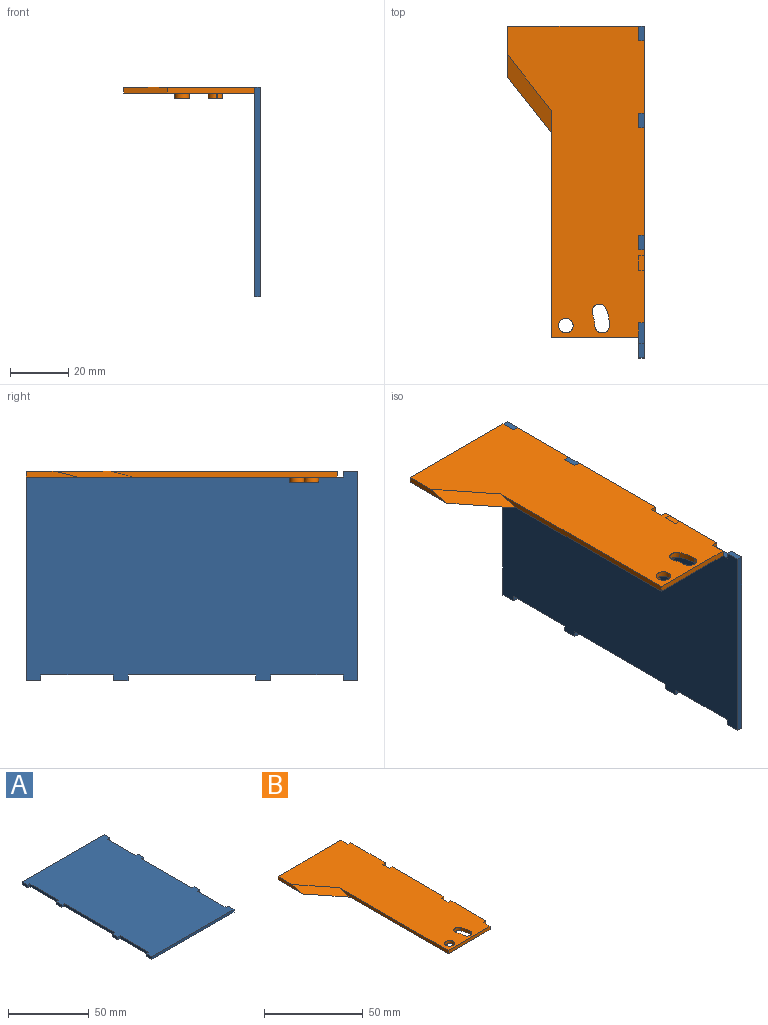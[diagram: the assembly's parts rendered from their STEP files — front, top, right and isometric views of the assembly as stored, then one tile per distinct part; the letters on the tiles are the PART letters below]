
ASSEMBLY  parts=2 mates=1
PART A: 30 faces, bbox 72x114x2 mm
  f0: plane 2x2mm, normal (0,1,0), area 4mm2, adj f1,f27,f28,f29
  f1: plane 44x2mm, normal (1,0,0), area 88mm2, adj f0,f2,f28,f29
  f2: plane 2x2mm, normal (0,-1,0), area 4mm2, adj f1,f3,f28,f29
  f3: plane 5x2mm, normal (1,0,0), area 10mm2, adj f2,f4,f28,f29
  f4: plane 2x2mm, normal (0,1,0), area 4mm2, adj f3,f5,f28,f29
  f5: plane 25x2mm, normal (1,0,0), area 50mm2, adj f4,f6,f28,f29
  f6: plane 2x2mm, normal (0,-1,0), area 4mm2, adj f5,f7,f28,f29
  f7: plane 5x2mm, normal (1,0,0), area 10mm2, adj f6,f8,f28,f29
  f8: plane 72x2mm, normal (0,1,0), area 144mm2, adj f7,f9,f28,f29
  f9: plane 5x2mm, normal (-1,0,0), area 10mm2, adj f8,f10,f28,f29
  f10: plane 2x2mm, normal (0,-1,0), area 4mm2, adj f9,f11,f28,f29
  f11: plane 25x2mm, normal (-1,0,0), area 50mm2, adj f10,f12,f28,f29
  f12: plane 2x2mm, normal (0,1,0), area 4mm2, adj f11,f13,f28,f29
  f13: plane 5x2mm, normal (-1,0,0), area 10mm2, adj f12,f14,f28,f29
  f14: plane 2x2mm, normal (0,-1,0), area 4mm2, adj f13,f15,f28,f29
  f15: plane 44x2mm, normal (-1,0,0), area 88mm2, adj f14,f16,f28,f29
  f16: plane 2x2mm, normal (0,1,0), area 4mm2, adj f15,f17,f28,f29
  f17: plane 5x2mm, normal (-1,0,0), area 10mm2, adj f16,f18,f28,f29
  f18: plane 2x2mm, normal (0,-1,0), area 4mm2, adj f17,f19,f28,f29
  f19: plane 25x2mm, normal (-1,0,0), area 50mm2, adj f18,f20,f28,f29
  f20: plane 2x2mm, normal (0,1,0), area 4mm2, adj f19,f21,f28,f29
  f21: plane 5x2mm, normal (-1,0,0), area 10mm2, adj f20,f22,f28,f29
  f22: plane 72x2mm, normal (0,-1,0), area 144mm2, adj f21,f23,f28,f29
  f23: plane 5x2mm, normal (1,0,0), area 10mm2, adj f22,f24,f28,f29
  f24: plane 2x2mm, normal (0,1,0), area 4mm2, adj f23,f25,f28,f29
  f25: plane 25x2mm, normal (1,0,0), area 50mm2, adj f24,f26,f28,f29
  f26: plane 2x2mm, normal (0,-1,0), area 4mm2, adj f25,f27,f28,f29
  f27: plane 5x2mm, normal (1,0,0), area 10mm2, adj f0,f26,f28,f29
  f28: plane 114x72mm, normal (0,0,1), area 7832mm2, adj f0,f1,f2,f3,f4,f5,f6,f7
  f29: plane 114x72mm, normal (0,0,-1), area 7832mm2, adj f0,f1,f2,f3,f4,f5,f6,f7
PART B: 30 faces, bbox 47x107x4 mm
  f0: plane 107x47mm, normal (0,0,1), area 3611.1mm2, adj f2,f3,f4,f5,f6,f7,f8,f9
  f1: plane 107x47mm, normal (0,0,-1), area 3688.7mm2, adj f2,f3,f4,f5,f6,f7,f8,f9
  f2: plane 78.07x2mm, normal (-1,0,0), area 148.3mm2, adj f0,f1,f3,f29
  f3: plane 30x2mm, normal (0,-1,0), area 60mm2, adj f0,f1,f2,f4
  f4: plane 5x2mm, normal (1,0,0), area 10mm2, adj f0,f1,f3,f5
  f5: plane 2x2mm, normal (0,-1,0), area 4mm2, adj f0,f1,f4,f6
  f6: plane 25x2mm, normal (1,0,0), area 50mm2, adj f0,f1,f5,f7
  f7: plane 2x2mm, normal (0,1,0), area 4mm2, adj f0,f1,f6,f8
  f8: plane 5x2mm, normal (1,0,0), area 10mm2, adj f0,f1,f7,f9
  f9: plane 2x2mm, normal (0,-1,0), area 4mm2, adj f0,f1,f8,f10
  f10: plane 37x2mm, normal (1,0,0), area 74mm2, adj f0,f1,f9,f11
  f11: plane 2x2mm, normal (0,1,0), area 4mm2, adj f0,f1,f10,f12
  f12: plane 5x2mm, normal (1,0,0), area 10mm2, adj f0,f1,f11,f13
  f13: plane 2x2mm, normal (0,-1,0), area 4mm2, adj f0,f1,f12,f14
  f14: plane 25x2mm, normal (1,0,0), area 50mm2, adj f0,f1,f13,f15
  f15: plane 2x2mm, normal (0,1,0), area 4mm2, adj f0,f1,f14,f16
  f16: plane 5x2mm, normal (1,0,0), area 10mm2, adj f0,f1,f15,f17
  f17: plane 45x2mm, normal (0,1,0), area 90mm2, adj f0,f1,f16,f18
  f18: plane 17.72x2mm, normal (-1,0,0), area 27.7mm2, adj f0,f1,f17,f29
  f19: cylinder r=2.5mm len=5mm, axis (0,0,1), area 31.4mm2, adj f1,f20
  f20: plane 5x5mm, normal (0,0,-1), area 19.6mm2, adj f19
  f21: cylinder r=2.5mm len=5mm, axis (0,0,1), area 30.6mm2, adj f1,f22,f23
  f22: cylinder r=2.5mm len=2mm, axis (0,0,1), area 0.8mm2, adj f1,f21,f23
  f23: plane 5x5mm, normal (0,0,-1), area 19.6mm2, adj f21,f22
  f24: cylinder r=10mm len=3.91mm, axis (0,0,-1), area 8mm2, adj f0,f1,f25,f27
  f25: cylinder r=2.5mm len=5mm, axis (0,0,-1), area 15.7mm2, adj f0,f1,f24,f26
  f26: cylinder r=15mm len=5.86mm, axis (0,0,-1), area 12mm2, adj f0,f1,f25,f27
  f27: cylinder r=2.5mm len=4.8mm, axis (0,0,-1), area 15.7mm2, adj f0,f1,f24,f26
  f28: cylinder r=2.5mm len=5mm, axis (0,0,-1), area 31.4mm2, adj f0,f1
  f29: plane 26.79x15mm, normal (-0.3,-0.24,0.92), area 126.5mm2, adj f0,f1,f2,f18
PLACE A rot(axis=(0,1,0),90deg) t=(16.57,-15.35,-35.18)mm
PLACE B t=(-8.43,-50.14,0)mm
MATE fastened A.f29 <-> B.f16  axis (-1,0,0) through (16.57,47.86,2)mm
